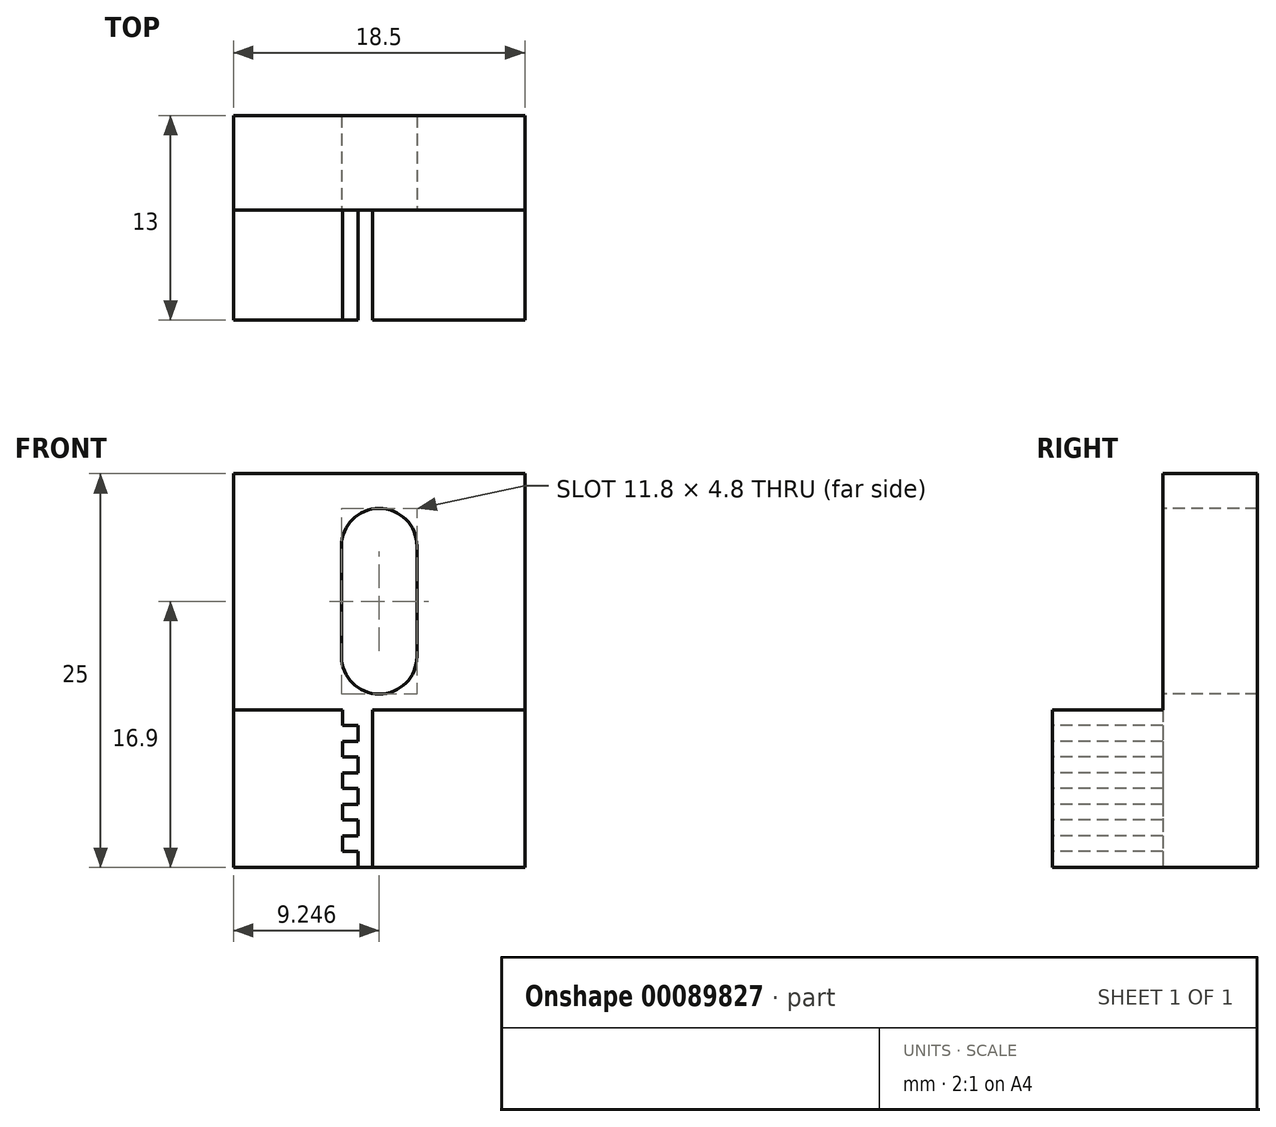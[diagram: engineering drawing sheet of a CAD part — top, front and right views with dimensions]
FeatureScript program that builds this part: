
annotation { "Feature Type Name" : "Feature", "Feature Type Description" : "" }
export const myFeature = defineFeature(function(context is Context, id is Id, definition is map)
    precondition{}
    {
        {
            var Q0;
            Q0=qCreatedBy(makeId("Top.planeOp"),FACE);
            var sketch = newSketch(context, id + "F0", { "sketchPlane" : qUnion([Q0])});
            skLineSegment(sketch, "E0.bottom", {"start": v(-4.96, 0) * mm, "end": v(13.54, 0) * mm});
            skLineSegment(sketch, "E0.top", {"start": v(-4.96, 25) * mm, "end": v(13.54, 25) * mm});
            skLineSegment(sketch, "E0.left", {"start": v(-4.96, 0) * mm, "end": v(-4.96, 25) * mm});
            skLineSegment(sketch, "E0.right", {"start": v(13.54, 0) * mm, "end": v(13.54, 25) * mm});
            skLineSegment(sketch, "E1", {"start": v(-4.96, 5) * mm, "end": v(13.54, 5) * mm});
            skLineSegment(sketch, "E2.bottom", {"start": v(-4.96, 17.95) * mm, "end": v(-1.96, 17.95) * mm});
            skLineSegment(sketch, "E2.top", {"start": v(-4.96, 12.05) * mm, "end": v(-1.96, 12.05) * mm});
            skLineSegment(sketch, "E2.left", {"start": v(-4.96, 17.95) * mm, "end": v(-4.96, 12.05) * mm});
            skLineSegment(sketch, "E2.right", {"start": v(-1.96, 17.95) * mm, "end": v(-1.96, 12.05) * mm});
            skLineSegment(sketch, "E3.bottom", {"start": v(13.54, 17.95) * mm, "end": v(10.54, 17.95) * mm});
            skLineSegment(sketch, "E3.top", {"start": v(13.54, 12.05) * mm, "end": v(10.54, 12.05) * mm});
            skLineSegment(sketch, "E3.left", {"start": v(13.54, 17.95) * mm, "end": v(13.54, 12.05) * mm});
            skLineSegment(sketch, "E3.right", {"start": v(10.54, 17.95) * mm, "end": v(10.54, 12.05) * mm});
            skPoint(sketch, "E4", {"position": v(-1.96, 15) * mm});
            skPoint(sketch, "E5", {"position": v(-4.96, 15) * mm});
            skLineSegment(sketch, "E6", {"start": v(-4.96, 15) * mm, "end": v(13.54, 15) * mm});
            skLineSegment(sketch, "E7", {"start": v(-4.96, 13) * mm, "end": v(13.54, 13) * mm});
            skSolve(sketch);
        }
        {
            var Q0;
            {var subQ0=sQuery(id+"F0.wireOp",EDGE,"E0.bottom");Q0=makeQuery(id+"F0.imprint","IMPRINT",FACE,{"disambiguationData":[TD([[makeQuery(id+"F0.imprint","IMPRINT",EDGE,{"derivedFrom":subQ0}),1.0]])]});}
            var Q1;
            {var subQ0=sQuery(id+"F0.wireOp",EDGE,"E1");Q1=makeQuery(id+"F0.imprint","IMPRINT",FACE,{"disambiguationData":[TD([[makeQuery(id+"F0.imprint","IMPRINT",EDGE,{"derivedFrom":subQ0}),1.0]])]});}
            var Q2;
            {var subQ0=sQuery(id+"F0.wireOp",EDGE,"E2.top");Q2=makeQuery(id+"F0.imprint","IMPRINT",FACE,{"disambiguationData":[TD([[makeQuery(id+"F0.imprint","IMPRINT",EDGE,{"derivedFrom":subQ0}),1.0]])]});}
            var Q3;
            {var subQ0=sQuery(id+"F0.wireOp",EDGE,"E3.top");Q3=makeQuery(id+"F0.imprint","IMPRINT",FACE,{"disambiguationData":[TD([[makeQuery(id+"F0.imprint","IMPRINT",EDGE,{"derivedFrom":subQ0}),-1.0]])]});}
            extrude(context, id + "F1", {"entities" : qUnion([Q0, Q1, Q2, Q3]), "depth" : 10 * mm});
        }
        {
            var Q0;
            Q0=makeQuery(id+"F1.opExtrude","SWEPT_FACE",FACE,{"disambiguationData":[OSD([sQuery(id+"F0.wireOp",EDGE,"E0.bottom")])]});
            var sketch = newSketch(context, id + "F2", { "sketchPlane" : qUnion([Q0])});
            skLineSegment(sketch, "E8", {"start": v(1.96, 10) * mm, "end": v(1.96, 9) * mm});
            skLineSegment(sketch, "E9", {"start": v(1.96, 9) * mm, "end": v(2.96, 9) * mm});
            skLineSegment(sketch, "E10", {"start": v(2.96, 9) * mm, "end": v(2.96, 8) * mm});
            skLineSegment(sketch, "E11", {"start": v(2.96, 8) * mm, "end": v(1.96, 8) * mm});
            skLineSegment(sketch, "E12", {"start": v(1.96, 8) * mm, "end": v(1.96, 7) * mm});
            skLineSegment(sketch, "E13", {"start": v(1.96, 7) * mm, "end": v(2.96, 7) * mm});
            skLineSegment(sketch, "E14", {"start": v(2.96, 7) * mm, "end": v(2.96, 6) * mm});
            skLineSegment(sketch, "E15", {"start": v(2.96, 6) * mm, "end": v(1.96, 6) * mm});
            skLineSegment(sketch, "E16", {"start": v(1.96, 6) * mm, "end": v(1.96, 5) * mm});
            skLineSegment(sketch, "E17", {"start": v(1.96, 5) * mm, "end": v(2.96, 5) * mm});
            skLineSegment(sketch, "E18", {"start": v(2.96, 5) * mm, "end": v(2.96, 4) * mm});
            skLineSegment(sketch, "E19", {"start": v(2.96, 4) * mm, "end": v(1.96, 4) * mm});
            skLineSegment(sketch, "E20", {"start": v(1.96, 4) * mm, "end": v(1.96, 3) * mm});
            skLineSegment(sketch, "E21", {"start": v(1.96, 3) * mm, "end": v(2.96, 3) * mm});
            skLineSegment(sketch, "E22", {"start": v(2.96, 3) * mm, "end": v(2.96, 2) * mm});
            skLineSegment(sketch, "E23", {"start": v(2.96, 2) * mm, "end": v(1.96, 2) * mm});
            skLineSegment(sketch, "E24", {"start": v(1.96, 2) * mm, "end": v(1.96, 1) * mm});
            skLineSegment(sketch, "E25", {"start": v(1.96, 1) * mm, "end": v(2.96, 1) * mm});
            skLineSegment(sketch, "E26", {"start": v(2.96, 1) * mm, "end": v(2.96, 0) * mm});
            skLineSegment(sketch, "E27", {"start": v(2.96, 0) * mm, "end": v(1.96, 0) * mm});
            skLineSegment(sketch, "E28", {"start": v(3.86, 10) * mm, "end": v(3.86, 0) * mm});
            skLineSegment(sketch, "E29", {"start": v(1.96, 10) * mm, "end": v(3.86, 10) * mm});
            skLineSegment(sketch, "E30", {"start": v(3.86, 0) * mm, "end": v(2.96, 0) * mm});
            skSolve(sketch);
        }
        {
            var Q0;
            Q0=makeQuery(id+"F2.imprint","IMPRINT",FACE,{"disambiguationData":[TD([[makeQuery(id+"F2.imprint","IMPRINT",EDGE,{"derivedFrom":sQuery(id+"F2.wireOp",EDGE,"E8")}),1.0]])]});
            extrude(context, id + "F3", {"entities" : qUnion([Q0]), "operationType" : NewBodyOperationType.REMOVE, "oppositeDirection" : true, "depth" : 7 * mm});
        }
        {
            var Q0;
            Q0=makeQuery(id+"F1.opExtrude","CAP_FACE",FACE,{"disambiguationData":[OSD([sQuery(id+"F0.wireOp",EDGE,"E0.bottom"),sQuery(id+"F0.wireOp",EDGE,"E0.left"),sQuery(id+"F0.wireOp",EDGE,"E0.right"),sQuery(id+"F0.wireOp",EDGE,"E7")])],"isStart":false});
            var sketch = newSketch(context, id + "F4", { "sketchPlane" : qUnion([Q0])});
            skLineSegment(sketch, "E31.bottom", {"start": v(-4.96, 0) * mm, "end": v(13.54, 0) * mm});
            skLineSegment(sketch, "E31.top", {"start": v(-4.96, 7) * mm, "end": v(13.54, 7) * mm});
            skLineSegment(sketch, "E31.left", {"start": v(-4.96, 7) * mm, "end": v(-4.96, 0) * mm});
            skLineSegment(sketch, "E31.right", {"start": v(13.54, 7) * mm, "end": v(13.54, 0) * mm});
            skSolve(sketch);
        }
        {
            var Q0;
            {var subQ0=makeQuery(id+"F1.opExtrude","CAP_EDGE",EDGE,{"disambiguationData":[OSD([sQuery(id+"F0.wireOp",EDGE,"E7")])],"isStart":false});Q0=makeQuery(id+"F4.imprint","IMPRINT",FACE,{"disambiguationData":[TD([[makeQuery(id+"F4.imprint","IMPRINT",EDGE,{"derivedFrom":subQ0}),-1.0]])]});}
            extrude(context, id + "F5", {"entities" : qUnion([Q0]), "operationType" : NewBodyOperationType.ADD, "depth" : 15 * mm});
        }
        {
            var Q0;
            Q0=makeQuery(id+"F5.boolean.opBoolean","MERGE",FACE,{"derivedFrom":[makeQuery(id+"F3.boolean.opBoolean","COPY",FACE,{"derivedFrom":makeQuery(id+"F3.opExtrude","CAP_FACE",FACE,{"disambiguationData":[OSD([sQuery(id+"F2.wireOp",EDGE,"E8"),sQuery(id+"F2.wireOp",EDGE,"E9"),sQuery(id+"F2.wireOp",EDGE,"E10"),sQuery(id+"F2.wireOp",EDGE,"E11"),sQuery(id+"F2.wireOp",EDGE,"E12"),sQuery(id+"F2.wireOp",EDGE,"E13"),sQuery(id+"F2.wireOp",EDGE,"E14"),sQuery(id+"F2.wireOp",EDGE,"E15"),sQuery(id+"F2.wireOp",EDGE,"E16"),sQuery(id+"F2.wireOp",EDGE,"E17"),sQuery(id+"F2.wireOp",EDGE,"E18"),sQuery(id+"F2.wireOp",EDGE,"E19"),sQuery(id+"F2.wireOp",EDGE,"E20"),sQuery(id+"F2.wireOp",EDGE,"E21"),sQuery(id+"F2.wireOp",EDGE,"E22"),sQuery(id+"F2.wireOp",EDGE,"E23"),sQuery(id+"F2.wireOp",EDGE,"E24"),sQuery(id+"F2.wireOp",EDGE,"E25"),sQuery(id+"F2.wireOp",EDGE,"E26"),sQuery(id+"F2.wireOp",EDGE,"E28"),sQuery(id+"F2.wireOp",EDGE,"E29"),sQuery(id+"F2.wireOp",EDGE,"E30")])],"isStart":false})}),makeQuery(id+"F5.opExtrude","SWEPT_FACE",FACE,{"disambiguationData":[OSD([sQuery(id+"F4.wireOp",EDGE,"E31.top")])]})]});
            var sketch = newSketch(context, id + "F6", { "sketchPlane" : qUnion([Q0])});
            skArc(sketch, "E32", {"start": v(6.69, 20.4) * mm, "mid": v(4.29, 22.8) * mm, "end": v(1.89, 20.4) * mm});
            skArc(sketch, "E33", {"start": v(1.89, 13.4) * mm, "mid": v(4.29, 11) * mm, "end": v(6.69, 13.4) * mm});
            skLineSegment(sketch, "E34", {"start": v(1.89, 20.4) * mm, "end": v(1.89, 13.4) * mm});
            skLineSegment(sketch, "E35", {"start": v(6.69, 20.4) * mm, "end": v(6.69, 13.4) * mm});
            skPoint(sketch, "E36", {"position": v(4.29, 25) * mm});
            skLineSegment(sketch, "E37", {"start": v(4.29, 10) * mm, "end": v(4.29, 11) * mm});
            skLineSegment(sketch, "E38", {"start": v(4.29, 22.8) * mm, "end": v(4.29, 25) * mm});
            skSolve(sketch);
        }
        {
            var Q0;
            Q0=qSketchRegion(id+"F6",true);
            extrude(context, id + "F7", {"entities" : qUnion([Q0]), "operationType" : NewBodyOperationType.REMOVE, "oppositeDirection" : true, "depth" : 25 * mm});
        }
    });
